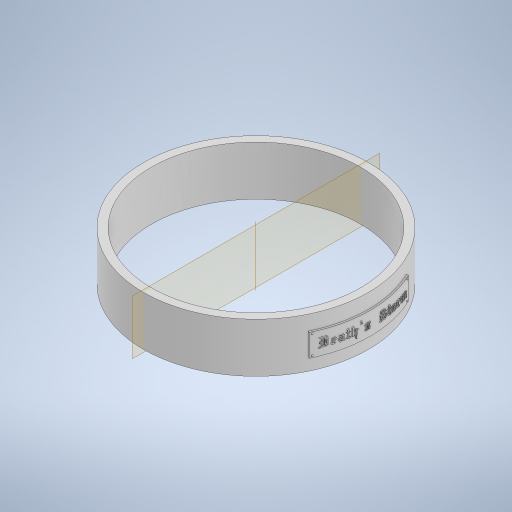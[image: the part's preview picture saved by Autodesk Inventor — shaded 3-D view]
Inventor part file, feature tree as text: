
AUTODESK INVENTOR PART (.ipt)
format: ipt  version: 2023 (Build 270158000, 158)  size: 5,349,376 bytes
history: native  units: in
note: dims shown in document units (in); Inventor stores cm internally (conversion verified against a paired STEP export)
features: emboss x3, pattern_circular x3, other x2, extrude x1, plane x1, fillet x1, sketch x1
ambient origin geometry x8: Origin, YZ Plane, XZ Plane, XY Plane, X Axis, Y Axis, Z Axis, Center Point
bodies: Solid1 (feature_tree)
feature tree (12):
  extrude  "Extrusion1"  Depth=0.3937in
  plane  "Work Plane1"
  other  "Text"
  emboss  "Emboss4"
  emboss  "Emboss5"
  emboss  "Emboss6"
  fillet  "Rivots"  Radius=0.8661in
  pattern_circular  "Circular Pattern1"  Count=6  [1 undecoded]
  pattern_circular  "Circular Pattern2"  [2 undecoded]
  pattern_circular  "Circular Pattern3"  [2 undecoded]
  sketch  "Sketch1"  dims[d0=3.937in d1=3.6614in d2=0.8661in d3=0.0in d4=2.3622in d6=0.4546in d10=0.0in d11=0.3937in d12=1.7717in d19=0.0in d20=0.0in d21=0.0295in d22=0.0in d23=0.0197in d24=0.0in d25=0.0295in d26=0.0295in d27=0.0295in d28=0.0157in d29=0.0in d30=0.0138in d31=0.7874in d32=360.0deg d34=0.7874in d35=360.0deg d37=0.7874in d38=360.0deg d33=0.0in]
  other  "NamePlate"
note: 5 required parameter values undecoded (feature->parameter linkage not recoverable at this tier; creation-order binding heuristic only, values carry confidence <= 0.55)
